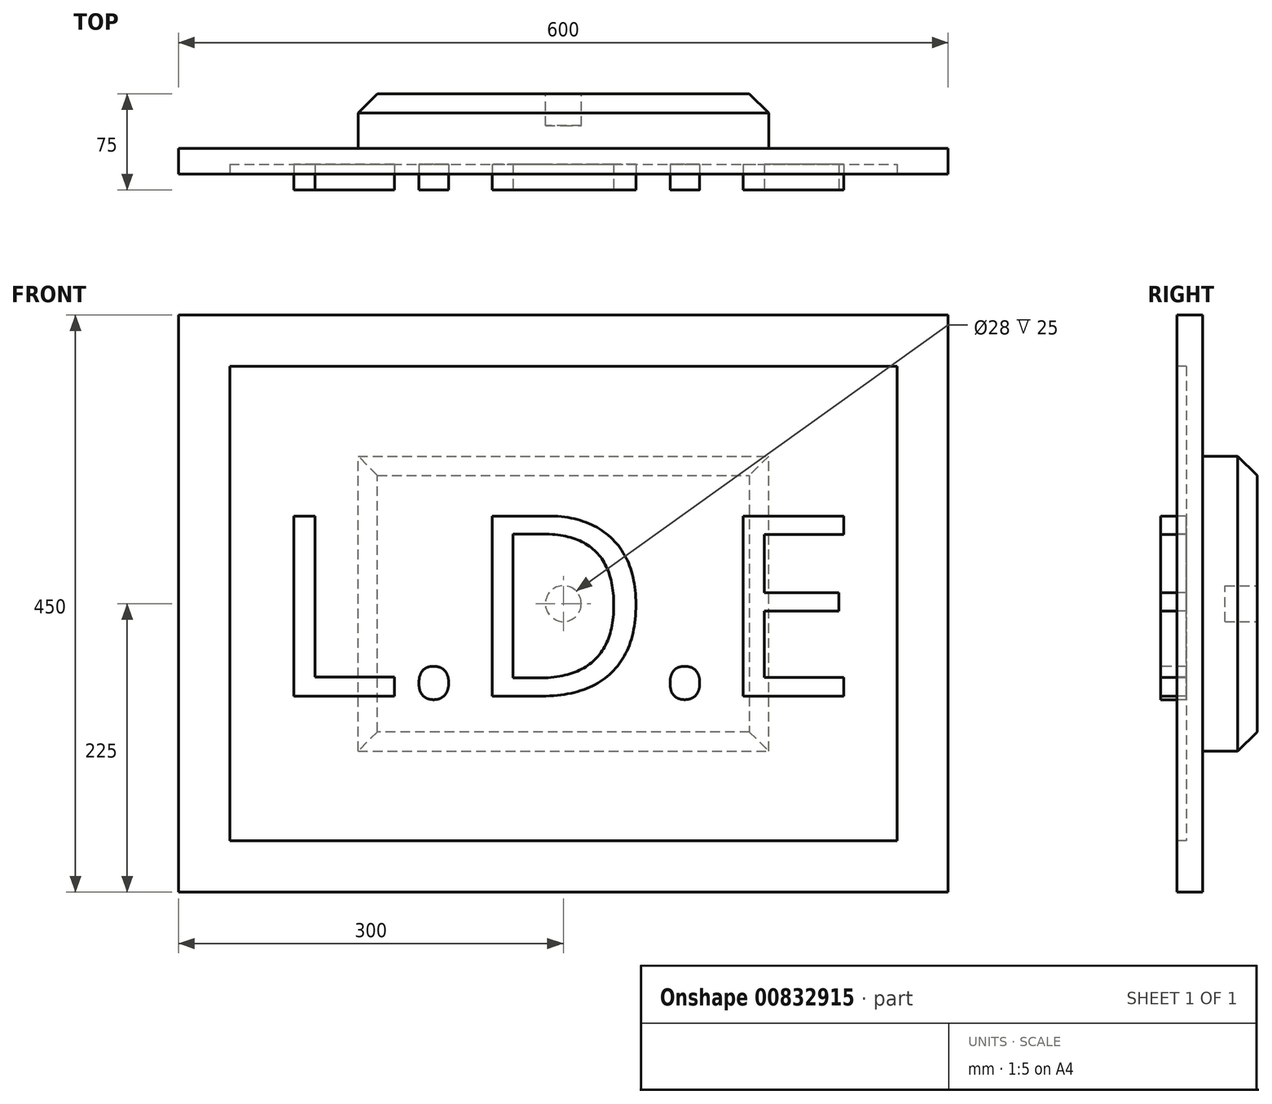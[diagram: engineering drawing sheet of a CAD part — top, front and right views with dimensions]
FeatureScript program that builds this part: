
annotation { "Feature Type Name" : "Feature", "Feature Type Description" : "" }
export const myFeature = defineFeature(function(context is Context, id is Id, definition is map)
    precondition{}
    {
        {
            var Q0;
            Q0=qCreatedBy(makeId("Top.planeOp"),FACE);
            var sketch = newSketch(context, id + "F0", { "sketchPlane" : qUnion([Q0])});
            skLineSegment(sketch, "E0.bottom", {"start": v(-300, 37.44) * mm, "end": v(300, 37.44) * mm});
            skLineSegment(sketch, "E0.top", {"start": v(-300, 17.44) * mm, "end": v(300, 17.44) * mm});
            skLineSegment(sketch, "E0.left", {"start": v(-300, 37.44) * mm, "end": v(-300, 17.44) * mm});
            skLineSegment(sketch, "E0.right", {"start": v(300, 37.44) * mm, "end": v(300, 17.44) * mm});
            skSolve(sketch);
        }
        {
            var Q0;
            Q0 = qSketchRegion(id + "F0", true);
            extrude(context, id + "F1", {"entities" : qUnion([Q0]), "depth" : 450 * mm, "offsetDistance" : 25 * mm});
        }
        {
            var Q0;
            Q0=qCreatedBy(makeId("Front.planeOp"),FACE);
            var sketch = newSketch(context, id + "F2", { "sketchPlane" : qUnion([Q0])});
            skLineSegment(sketch, "E1.bottom", {"start": v(-260, 410) * mm, "end": v(260, 410) * mm});
            skLineSegment(sketch, "E1.top", {"start": v(-260, 40) * mm, "end": v(260, 40) * mm});
            skLineSegment(sketch, "E1.left", {"start": v(-260, 410) * mm, "end": v(-260, 40) * mm});
            skLineSegment(sketch, "E1.right", {"start": v(260, 410) * mm, "end": v(260, 40) * mm});
            skSolve(sketch);
        }
        {
            var Q0;
            Q0 = qSketchRegion(id + "F2", true);
            extrude(context, id + "F3", {"entities" : qUnion([Q0]), "operationType" : NewBodyOperationType.REMOVE, "oppositeDirection" : true, "depth" : 25 * mm, "offsetDistance" : 25 * mm});
        }
        {
            var Q0;
            Q0=qCreatedBy(makeId("Front.planeOp"),FACE);
            cPlane(context, id + "F4", {"entities" : qUnion([Q0]), "cplaneType" : CPlaneType.OFFSET, "offset" : 80 * mm, "oppositeDirection" : true, "width" : 150 * mm, "height" : 150 * mm});
        }
        {
            var Q0;
            Q0=qCreatedBy(id+"F4.planeOp",FACE);
            var sketch = newSketch(context, id + "F5", { "sketchPlane" : qUnion([Q0])});
            skLineSegment(sketch, "E2.bottom", {"start": v(160, 340) * mm, "end": v(-160, 340) * mm});
            skLineSegment(sketch, "E2.top", {"start": v(160, 110) * mm, "end": v(-160, 110) * mm});
            skLineSegment(sketch, "E2.left", {"start": v(160, 340) * mm, "end": v(160, 110) * mm});
            skLineSegment(sketch, "E2.right", {"start": v(-160, 340) * mm, "end": v(-160, 110) * mm});
            skSolve(sketch);
        }
        {
            var Q0;
            Q0=makeQuery(id+"F5.imprint","IMPRINT",FACE,{"disambiguationData":[TD([[makeQuery(id+"F5.imprint","IMPRINT",EDGE,{"derivedFrom":sQuery(id+"F5.wireOp",EDGE,"E2.bottom")}),1.0]])]});
            extrude(context, id + "F6", {"entities" : qUnion([Q0]), "operationType" : NewBodyOperationType.ADD, "endBound" : BoundingType.UP_TO_NEXT, "depth" : 25 * mm, "offsetDistance" : 25 * mm});
        }
        {
            var Q0;
            Q0=makeQuery(id+"F6.opExtrude","CAP_EDGE",EDGE,{"disambiguationData":[OSD([sQuery(id+"F5.wireOp",EDGE,"E2.left")])],"isStart":true});
            var Q1;
            Q1=makeQuery(id+"F6.opExtrude","CAP_EDGE",EDGE,{"disambiguationData":[OSD([sQuery(id+"F5.wireOp",EDGE,"E2.bottom")])],"isStart":true});
            var Q2;
            Q2=makeQuery(id+"F6.opExtrude","CAP_EDGE",EDGE,{"disambiguationData":[OSD([sQuery(id+"F5.wireOp",EDGE,"E2.right")])],"isStart":true});
            var Q3;
            Q3=makeQuery(id+"F6.opExtrude","CAP_FACE",FACE,{"disambiguationData":[OSD([sQuery(id+"F5.wireOp",EDGE,"E2.bottom"),sQuery(id+"F5.wireOp",EDGE,"E2.top"),sQuery(id+"F5.wireOp",EDGE,"E2.left"),sQuery(id+"F5.wireOp",EDGE,"E2.right")])],"isStart":true});
            chamfer(context, id + "F7", {"entities" : qUnion([Q0, Q1, Q2, Q3]), "width" : 15 * mm, "tangentPropagation" : true});
        }
        {
            var Q0;
            Q0=qCreatedBy(id+"F4.planeOp",FACE);
            var sketch = newSketch(context, id + "F8", { "sketchPlane" : qUnion([Q0])});
            skCircle(sketch, "E3", {"center": v(0, 225) * mm, "radius": 14 * mm});
            skSolve(sketch);
        }
        {
            var Q0;
            Q0 = qSketchRegion(id + "F8", true);
            extrude(context, id + "F9", {"entities" : qUnion([Q0]), "operationType" : NewBodyOperationType.REMOVE, "depth" : 25 * mm, "offsetDistance" : 25 * mm});
        }
        {
            var Q0;
            Q0=makeQuery(id+"F3.boolean.opBoolean","COPY",FACE,{"derivedFrom":makeQuery(id+"F3.opExtrude","CAP_FACE",FACE,{"disambiguationData":[OSD([sQuery(id+"F2.wireOp",EDGE,"E1.bottom"),sQuery(id+"F2.wireOp",EDGE,"E1.top"),sQuery(id+"F2.wireOp",EDGE,"E1.left"),sQuery(id+"F2.wireOp",EDGE,"E1.right")])],"isStart":false})});
            cPlane(context, id + "F10", {"entities" : qUnion([Q0]), "cplaneType" : CPlaneType.OFFSET, "offset" : 20 * mm, "width" : 150 * mm, "height" : 150 * mm});
        }
        {
            var Q0;
            Q0=qCreatedBy(id+"F10.planeOp",FACE);
            var sketch = newSketch(context, id + "F11", { "sketchPlane" : qUnion([Q0])});
            skText(sketch, "E4", { "text": "L.D.E", "fontName": "OpenSans-Regular.ttf"});
            const initialGuessF11  = {"E4": [-0.22925, 0.15292, 1, 0, 0.14161]};
            skSetInitialGuess(sketch, initialGuessF11);
            skSolve(sketch);
        }
        {
            var Q0;
            Q0 = qSketchRegion(id + "F11", true);
            extrude(context, id + "F12", {"entities" : qUnion([Q0]), "operationType" : NewBodyOperationType.ADD, "endBound" : BoundingType.UP_TO_NEXT, "oppositeDirection" : true, "depth" : 25 * mm, "offsetDistance" : 25 * mm});
        }
    });
